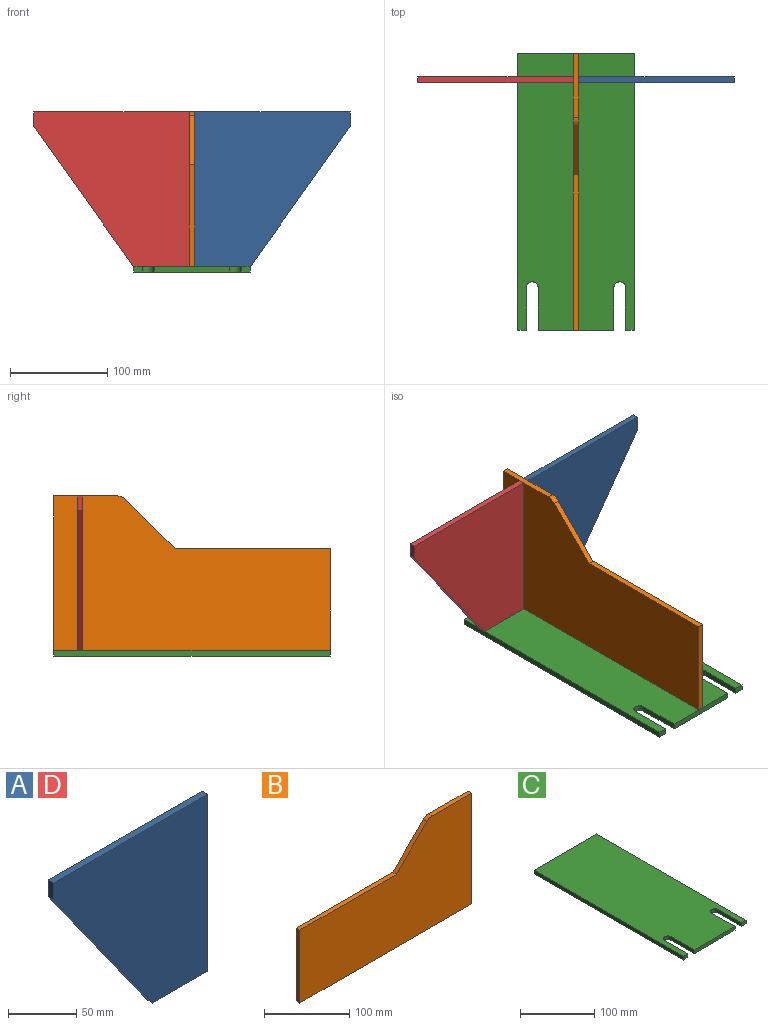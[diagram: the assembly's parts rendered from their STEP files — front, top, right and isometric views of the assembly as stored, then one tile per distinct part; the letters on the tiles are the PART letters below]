
ASSEMBLY  parts=4 mates=3
PART A: 7 faces, bbox 160x6x159 mm
  f0: plane 159x6mm, normal (1,0,0), area 954mm2, adj f1,f4,f5,f6
  f1: plane 160x6mm, normal (0,0,1), area 960mm2, adj f0,f2,f5,f6
  f2: plane 15x6mm, normal (-1,0,0), area 90mm2, adj f1,f3,f5,f6
  f3: plane 144x102.5mm, normal (-0.81,0,-0.58), area 1060.5mm2, adj f2,f4,f5,f6
  f4: plane 57.5x6mm, normal (0,0,-1), area 345mm2, adj f0,f3,f5,f6
  f5: plane 160x159mm, normal (0,-1,0), area 18060mm2, adj f0,f1,f2,f3,f4
  f6: plane 160x159mm, normal (0,1,0), area 18060mm2, adj f0,f1,f2,f3,f4
PART B: 9 faces, bbox 285x6x159 mm
  f0: plane 65.5x6mm, normal (0,0,1), area 393mm2, adj f1,f6,f7,f8
  f1: cylinder r=12.5mm len=8.84mm, axis (0,1,0), area 58.9mm2, adj f0,f2,f7,f8
  f2: plane 50.66x50.66mm, normal (-0.71,0,0.71), area 429.9mm2, adj f1,f3,f7,f8
  f3: plane 160x6mm, normal (0,0,1), area 960mm2, adj f2,f4,f7,f8
  f4: plane 104.68x6mm, normal (-1,0,0), area 628.1mm2, adj f3,f5,f7,f8
  f5: plane 285x6mm, normal (0,0,-1), area 1710mm2, adj f4,f6,f7,f8
  f6: plane 159x6mm, normal (1,0,0), area 954mm2, adj f0,f5,f7,f8
  f7: plane 285x159mm, normal (0,-1,0), area 35144.6mm2, adj f0,f1,f2,f3,f4,f5,f6
  f8: plane 285x159mm, normal (0,1,0), area 35144.6mm2, adj f0,f1,f2,f3,f4,f5,f6
PART C: 14 faces, bbox 120x285x6 mm
  f0: plane 78x6mm, normal (0,-1,0), area 468mm2, adj f1,f11,f12,f13
  f1: plane 44x6mm, normal (1,0,0), area 264mm2, adj f0,f2,f12,f13
  f2: cylinder r=6mm len=12mm, axis (0,0,-1), area 113.1mm2, adj f1,f3,f12,f13
  f3: plane 44x6mm, normal (-1,0,0), area 264mm2, adj f2,f4,f12,f13
  f4: plane 9x6mm, normal (0,-1,0), area 54mm2, adj f3,f5,f12,f13
  f5: plane 285x6mm, normal (1,0,0), area 1710mm2, adj f4,f6,f12,f13
  f6: plane 120x6mm, normal (0,1,0), area 720mm2, adj f5,f7,f12,f13
  f7: plane 285x6mm, normal (-1,0,0), area 1710mm2, adj f6,f8,f12,f13
  f8: plane 9x6mm, normal (0,-1,0), area 54mm2, adj f7,f9,f12,f13
  f9: plane 44x6mm, normal (1,0,0), area 264mm2, adj f8,f10,f12,f13
  f10: cylinder r=6mm len=12mm, axis (0,0,-1), area 113.1mm2, adj f9,f11,f12,f13
  f11: plane 44x6mm, normal (-1,0,0), area 264mm2, adj f0,f10,f12,f13
  f12: plane 285x120mm, normal (0,0,1), area 33030.9mm2, adj f0,f1,f2,f3,f4,f5,f6,f7
  f13: plane 285x120mm, normal (0,0,-1), area 33030.9mm2, adj f0,f1,f2,f3,f4,f5,f6,f7
PART D: same geometry as A
PLACE A rot(axis=(0,0,1),180deg) t=(12.37,28.07,65.21)mm
PLACE B rot(axis=(0,0,1),90deg) t=(-73.63,-84.43,65.21)mm
PLACE C t=(-70.63,-84.43,-20.29)mm
PLACE D t=(-153.63,34.07,65.21)mm
MATE fastened D.f0 <-> B.f8  axis (1,0,0) through (-73.63,28.07,144.71)mm
MATE fastened A.f0 <-> B.f7  axis (-1,0,0) through (-67.63,28.07,144.71)mm
MATE fastened B.f5 <-> C.f12  axis (0,0,-1) through (-70.63,-226.93,-14.29)mm
